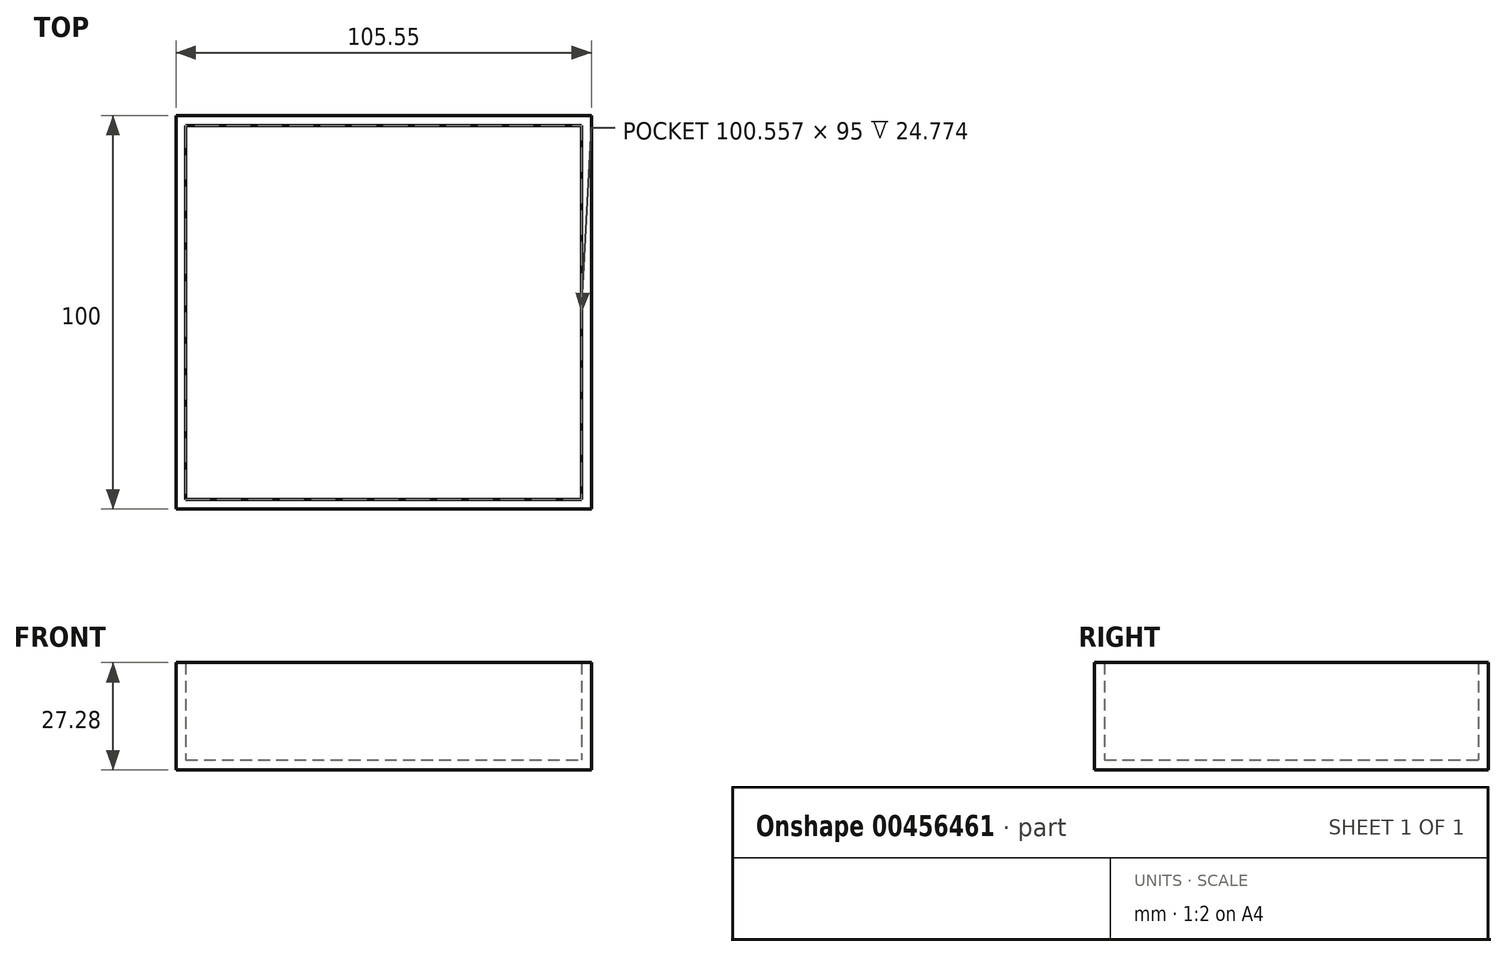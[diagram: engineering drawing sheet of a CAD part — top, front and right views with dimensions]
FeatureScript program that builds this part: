
annotation { "Feature Type Name" : "Feature", "Feature Type Description" : "" }
export const myFeature = defineFeature(function(context is Context, id is Id, definition is map)
    precondition{}
    {
        {
            var Q0;
            Q0=qCreatedBy(makeId("Front.planeOp"),FACE);
            var sketch = newSketch(context, id + "F0", { "sketchPlane" : qUnion([Q0])});
            skLineSegment(sketch, "E0.bottom", {"start": v(-55.13, 40.7) * mm, "end": v(50.42, 40.7) * mm});
            skLineSegment(sketch, "E0.top", {"start": v(-55.13, 13.43) * mm, "end": v(50.42, 13.43) * mm});
            skLineSegment(sketch, "E0.left", {"start": v(-55.13, 40.7) * mm, "end": v(-55.13, 13.43) * mm});
            skLineSegment(sketch, "E0.right", {"start": v(50.42, 40.7) * mm, "end": v(50.42, 13.43) * mm});
            skSolve(sketch);
        }
        {
            var Q0;
            Q0 = qSketchRegion(id + "F0", true);
            var Q1;
            Q1=makeQuery(id+"F0.imprint","IMPRINT",FACE,{"disambiguationData":[TD([[makeQuery(id+"F0.imprint","IMPRINT",EDGE,{"derivedFrom":sQuery(id+"F0.wireOp",EDGE,"E0.bottom")}),-1.0]])]});
            extrude(context, id + "F1", {"entities" : qUnion([Q0, Q1]), "depth" : 100 * mm});
        }
        {
            var Q0;
            Q0=makeQuery(id+"F1.opExtrude","SWEPT_FACE",FACE,{"disambiguationData":[OSD([sQuery(id+"F0.wireOp",EDGE,"E0.bottom")])]});
            var Q1;
            Q1=makeQuery(id+"F1.opExtrude","SWEPT_BODY",BODY,{"disambiguationData":[OSD([sQuery(id+"F0.wireOp",EDGE,"E0.bottom"),sQuery(id+"F0.wireOp",EDGE,"E0.top"),sQuery(id+"F0.wireOp",EDGE,"E0.left"),sQuery(id+"F0.wireOp",EDGE,"E0.right")])]});
            shell(context, id + "F2", {"entities" : qUnion([Q0]), "parts" : qUnion([Q1]), "thickness" : 2.5 * mm});
        }
    });
